# Revit family: Plumbing-Showerheads-Sloan-Valve-AC-11z
name_source: partatom
category: Plumbing Fixtures
units: mm (PartAtom-declared; Revit-internal decimal feet)

## family parameters
Cut with Voids When Loaded = No
Host = Face
OmniClass Number = 23.40.20.21
OmniClass Title = Toilet and Bath Specialties
Part Type = Normal
Room Calculation Point = No
Round Connector Dimension = Use Diameter
Shared = No

## types (6) — shared parameters
Assembly Code = D2010
Default Elevation = 8"
Depth = 2 1/2"
Edition number = 1
Height = 4 1/2"
Keynote = 15410
Manufacturer = Sloan Valve
Product data url = https://bimobject.com
URL = www.sloanvalve.com
Water Inlet Connection Diameter = 1"
Width = 2 1/2"

## per-type parameters (varying)
| type | Description | Part Number | Product Material | Water Flow |
| AC-11-2.0GPM-CP | Polished Chrome Finish, Act-O-Matic® Standard with Thumb Screw Volume Control Showerhead. | 4020130 | Sloan Valve - Finish - Polished Chrome | 2 GPM |
| AC-11-2.0GPM-CP-WWT | Polished Chrome Finish, Whitworth Thread, Act-O-Matic® Standard with Thumb Screw Volume Control Showerhead. | 4020131 | Sloan Valve - Finish - Polished Chrome | 2 GPM |
| AC-11-2.5GPM-BN | Brushed Nickel Finish, Act-O-Matic® Standard with Thumb Screw Volume Control Showerhead | 4020115 | Sloan Valve - Finish - Brushed Nickel | 3 GPM |
| AC-11-2.5GPM-CP | Polished Chrome Finish, Act-O-Matic® Standard with Thumb Screw Volume Control Showerhead. | 4020100 | Sloan Valve - Finish - Polished Chrome | 3 GPM |
| AC-11-2.5GPM-PB | Polished Brass Finish, Act-O-Matic® Standard with Thumb Screw Volume Control Showerhead. | 4020112 | Sloan Valve - Finish - Polished Brass | 3 GPM |
| AC-11-2.5GPM-SF | Brushed Stainless Finish, Act-O-Matic® Standard with Thumb Screw Volume Control Showerhead. | 4020116 | Sloan Valve - Stainless Steel - Brushed | 3 GPM |

note: column(s) folded — value = type name in every type: Model

## geometry (parser evidence)
native form markers: Sweep x2
no freeform markers — native parametric forms only
